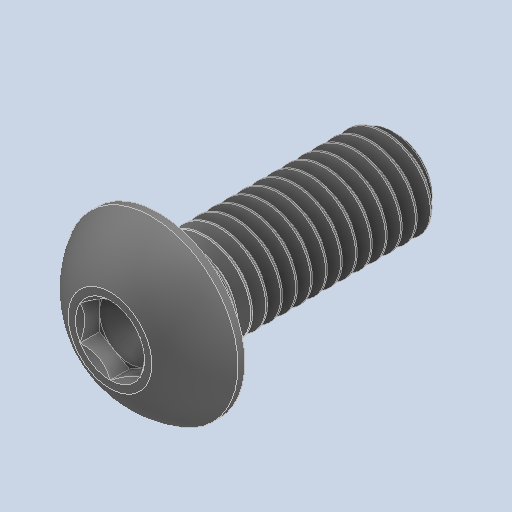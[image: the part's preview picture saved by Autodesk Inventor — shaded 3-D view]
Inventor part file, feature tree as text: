
AUTODESK INVENTOR PART (.ipt)
format: ipt  version: 2024.2 (Build 282272000, 272)  size: 549,376 bytes
history: native  units: in
note: dims shown in document units (in); Inventor stores cm internally (conversion verified against a paired STEP export)
features: revolve x1
ambient origin geometry x8: Origin, YZ Plane, XZ Plane, XY Plane, X Axis, Y Axis, Z Axis, Center Point
bodies: Solid1 (feature_tree)
feature tree (1):
  revolve  "Revolve2"  [1 undecoded]
note: 1 required parameter value undecoded (feature->parameter linkage not recoverable at this tier; creation-order binding heuristic only, values carry confidence <= 0.55)
